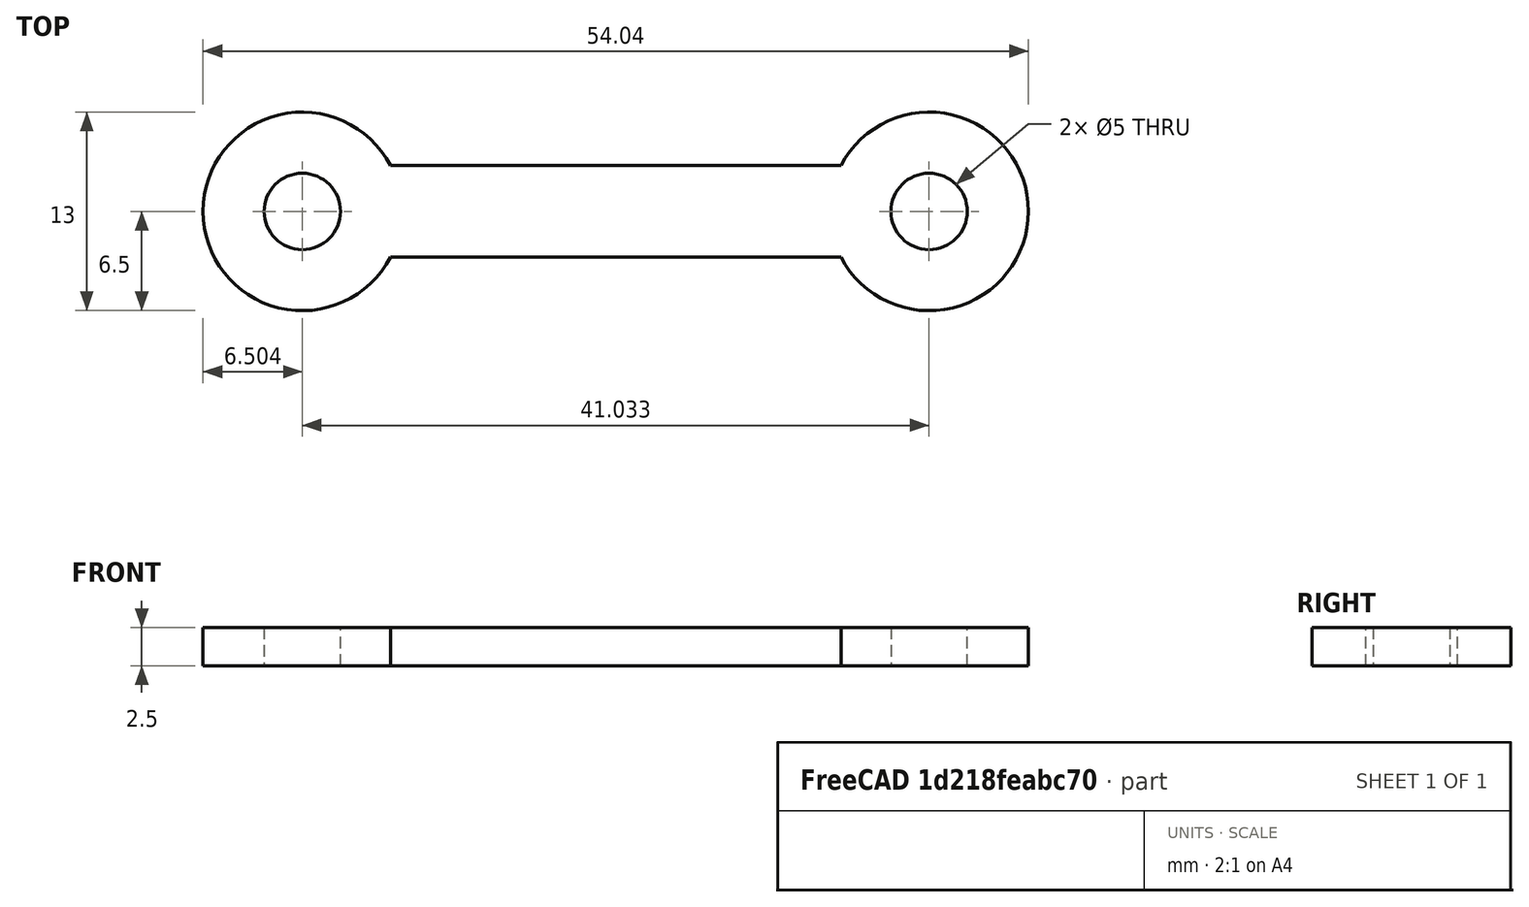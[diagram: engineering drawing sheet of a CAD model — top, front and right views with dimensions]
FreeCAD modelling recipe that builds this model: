
FCSTD DOCUMENT  (FreeCAD 0.15R4671 (Git))
Label: sensorBoard_fixTop
License: All rights reserved
LicenseURL: http://fr.wikipedia.org/wiki/<copyright redacted>
objects: Sketcher::SketchObject×1, PartDesign::Pad×1
note: 3 computed .brp shape members not serialized (recipe doc carries the construction recipe); baked Part::Feature solids carry a one-line shape summary decoded from their .brp

FEATURE [Sketcher::SketchObject] Sketch
  sketch-geometry (8):
    g0: LineSegment StartX=-14.75 StartY=3 StartZ=0 EndX=14.75 EndY=3 EndZ=0
    g1: LineSegment [constr] StartX=14.75 StartY=3 StartZ=0 EndX=14.75 EndY=-3 EndZ=0
    g2: LineSegment StartX=14.75 StartY=-3 StartZ=0 EndX=-14.75 EndY=-3 EndZ=0
    g3: LineSegment [constr] StartX=-14.75 StartY=-3 StartZ=0 EndX=-14.75 EndY=3 EndZ=0
    g4: Circle CenterX=-20.5163 CenterY=0 CenterZ=0 NormalX=0 NormalY=0 NormalZ=1 Radius=2.5
    g5: Circle CenterX=20.5163 CenterY=0 CenterZ=0 NormalX=0 NormalY=0 NormalZ=1 Radius=2.5
    g6: ArcOfCircle CenterX=-20.5163 CenterY=0 CenterZ=0 NormalX=0 NormalY=0 NormalZ=1 Radius=6.5 StartAngle=0.479729 EndAngle=5.80346
    g7: ArcOfCircle CenterX=20.5163 CenterY=0 CenterZ=0 NormalX=0 NormalY=0 NormalZ=1 Radius=6.5 StartAngle=3.62132 EndAngle=8.94505
  constraints (24):
    c: Coincident(g0,g1)
    c: Coincident(g1,g2)
    c: Coincident(g2,g3)
    c: Coincident(g3,g0)
    c: Horizontal(g0)
    c: Horizontal(g2)
    c: Vertical(g1)
    c: Vertical(g3)
    c: Distance(g0) = 29.5
    c: Distance(g3) = 6
    c: Radius(g5) = 2.5
    c: Equal(g5,g4)
    c: Symmetric(g2,g0,g-1)
    c: DistanceY(g4,g5) = 0
    c: PointOnObject(g4,g-1)
    c: Symmetric(g4,g5,g-1)
    c: Coincident(g6,g4)
    c: Coincident(g6,g0)
    c: Coincident(g6,g2)
    c: Coincident(g7,g5)
    c: Coincident(g7,g0)
    c: Coincident(g7,g1)
    c: Radius(g6) = 6.5
    c: Equal(g6,g7)
FEATURE [PartDesign::Pad] Pad
  Length = 2.5
  Length2 = 100
  Sketch = -> Sketch
  Type = 0
